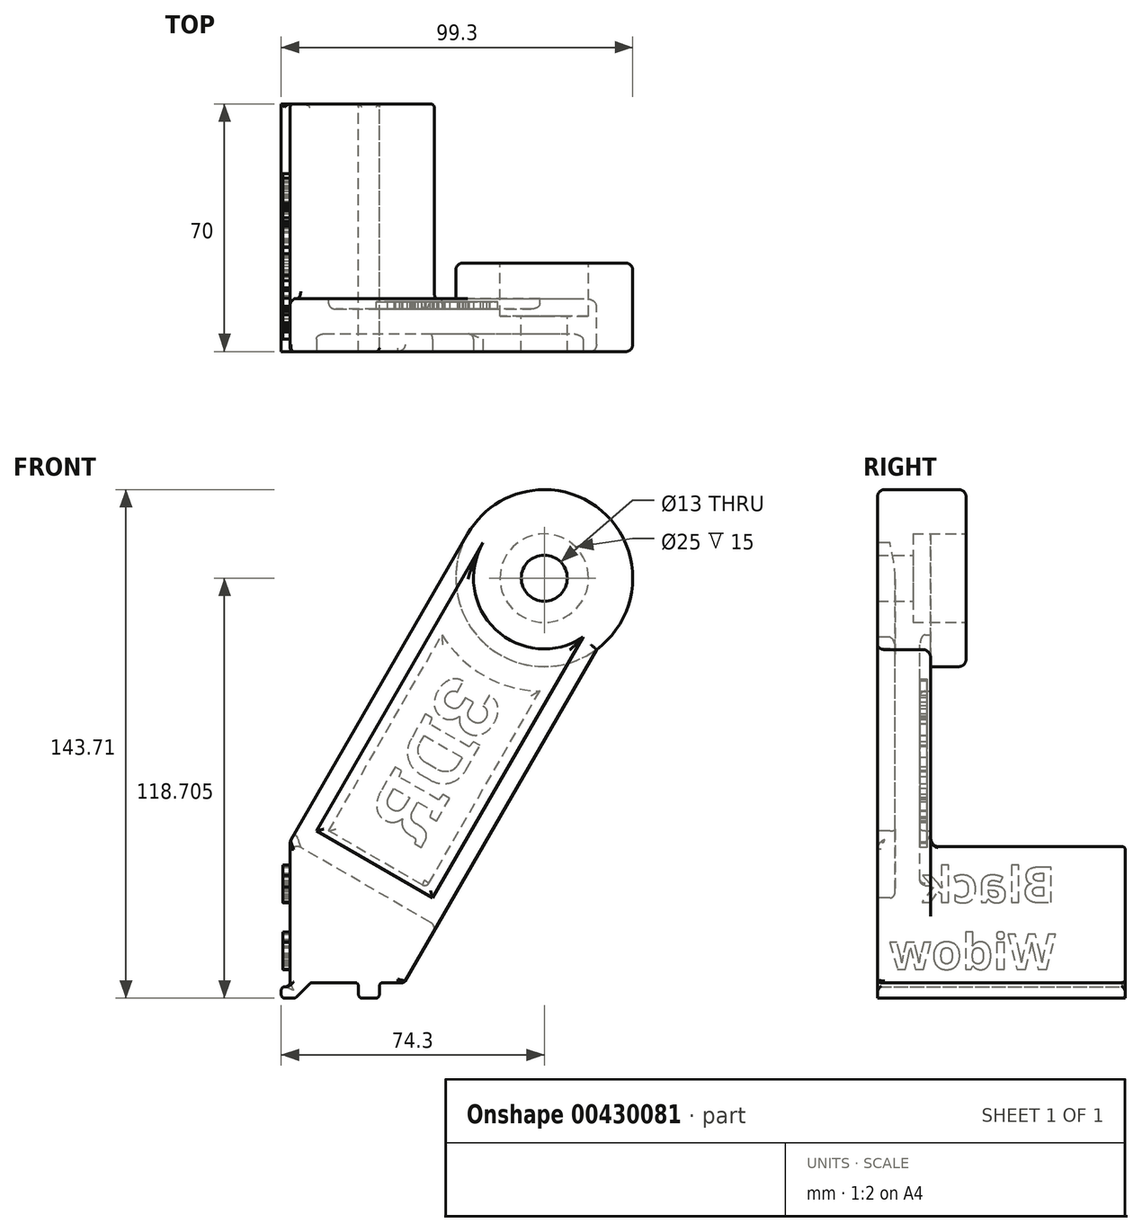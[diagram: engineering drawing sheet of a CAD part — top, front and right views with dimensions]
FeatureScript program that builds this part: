
annotation { "Feature Type Name" : "Feature", "Feature Type Description" : "" }
export const myFeature = defineFeature(function(context is Context, id is Id, definition is map)
    precondition{}
    {
        {
            var Q0;
            Q0=qCreatedBy(makeId("Front.planeOp"),FACE);
            var sketch = newSketch(context, id + "F0", { "sketchPlane" : qUnion([Q0])});
            skLineSegment(sketch, "E0", {"start": v(0, 0) * mm, "end": v(13.54, 0) * mm});
            skLineSegment(sketch, "E1", {"start": v(13.54, 0) * mm, "end": v(13.54, -4.39) * mm});
            skLineSegment(sketch, "E2", {"start": v(13.54, -4.39) * mm, "end": v(19.4, -4.39) * mm});
            skLineSegment(sketch, "E3", {"start": v(19.4, -4.39) * mm, "end": v(19.4, 0) * mm});
            skLineSegment(sketch, "E4", {"start": v(19.4, 0) * mm, "end": v(26.4, 0) * mm});
            skLineSegment(sketch, "E5", {"start": v(0, 0) * mm, "end": v(-4.4, -4.4) * mm});
            skLineSegment(sketch, "E6", {"start": v(-4.4, -4.4) * mm, "end": v(-8.3, -4.4) * mm});
            skLineSegment(sketch, "E7", {"start": v(-8.3, -4.4) * mm, "end": v(-8.3, -1.14) * mm});
            skLineSegment(sketch, "E8", {"start": v(-8.3, -1.14) * mm, "end": v(-5.8, -1.14) * mm});
            skLineSegment(sketch, "E9", {"start": v(-5.8, -1.14) * mm, "end": v(-5.8, 39.95) * mm});
            skLineSegment(sketch, "E10", {"start": v(26.4, 0) * mm, "end": v(80.74, 94.13) * mm});
            skLineSegment(sketch, "E11", {"start": v(0, 0) * mm, "end": v(66, 114.32) * mm, "construction": true});
            skCircle(sketch, "E12", {"center": v(66, 114.32) * mm, "radius": 95 * mm, "construction": true});
            skLineSegment(sketch, "E13", {"start": v(-5.8, 39.95) * mm, "end": v(44.35, 126.82) * mm});
            skCircle(sketch, "E14", {"center": v(66, 114.32) * mm, "radius": 6.5 * mm});
            skCircle(sketch, "E15", {"center": v(66, 114.32) * mm, "radius": 25 * mm});
            skSolve(sketch);
        }
        {
            var Q0;
            Q0 = qSketchRegion(id + "F0", true);
            extrude(context, id + "F1", {"entities" : qUnion([Q0]), "depth" : 70 * mm});
        }
        {
            var Q0;
            Q0=makeQuery(id+"F1.opExtrude","SWEPT_FACE",FACE,{"disambiguationData":[OSD([sQuery(id+"F0.wireOp",EDGE,"E13")])]});
            var sketch = newSketch(context, id + "F2", { "sketchPlane" : qUnion([Q0])});
            skLineSegment(sketch, "E16.0", {"start": v(70, 31.7) * mm, "end": v(70, 132) * mm, "construction": true});
            skLineSegment(sketch, "E17", {"start": v(55, 31.7) * mm, "end": v(55, 132) * mm});
            skLineSegment(sketch, "E18", {"start": v(55, 31.7) * mm, "end": v(0, 31.7) * mm});
            skLineSegment(sketch, "E19", {"start": v(0, 31.7) * mm, "end": v(0, 132) * mm});
            skLineSegment(sketch, "E20", {"start": v(0, 132) * mm, "end": v(0, 172) * mm});
            skLineSegment(sketch, "E21", {"start": v(0, 172) * mm, "end": v(55, 172) * mm});
            skLineSegment(sketch, "E22", {"start": v(55, 132) * mm, "end": v(55, 172) * mm});
            skSolve(sketch);
        }
        {
            var Q0;
            {var subQ0=sQuery(id+"F2.wireOp",EDGE,"E20");Q0=makeQuery(id+"F2.imprint","IMPRINT",FACE,{"disambiguationData":[TD([[makeQuery(id+"F2.imprint","IMPRINT",EDGE,{"derivedFrom":subQ0}),-1.0]])]});}
            var Q1;
            {var subQ0=sQuery(id+"F2.wireOp",EDGE,"E17");Q1=makeQuery(id+"F2.imprint","IMPRINT",FACE,{"disambiguationData":[TD([[makeQuery(id+"F2.imprint","IMPRINT",EDGE,{"derivedFrom":subQ0}),1.0]])]});}
            extrude(context, id + "F3", {"entities" : qUnion([Q0, Q1]), "operationType" : NewBodyOperationType.REMOVE, "endBound" : BoundingType.THROUGH_ALL, "oppositeDirection" : true, "depth" : 25 * mm});
        }
        {
            var Q0;
            Q0=makeQuery(id+"F3.boolean.opBoolean","COPY",FACE,{"derivedFrom":makeQuery(id+"F3.opExtrude","SWEPT_FACE",FACE,{"disambiguationData":[OSD([sQuery(id+"F2.wireOp",EDGE,"E17"),sQuery(id+"F2.wireOp",EDGE,"E22")])]})});
            var sketch = newSketch(context, id + "F4", { "sketchPlane" : qUnion([Q0])});
            skCircle(sketch, "E23", {"center": v(-66, 114.32) * mm, "radius": 25 * mm});
            skSolve(sketch);
        }
        {
            var Q0;
            Q0 = qSketchRegion(id + "F4", true);
            extrude(context, id + "F5", {"entities" : qUnion([Q0]), "operationType" : NewBodyOperationType.ADD, "depth" : 10 * mm});
        }
        {
            var Q0;
            Q0=makeQuery(id+"F5.opExtrude","CAP_FACE",FACE,{"disambiguationData":[OSD([sQuery(id+"F4.wireOp",EDGE,"E23")])],"isStart":false});
            var sketch = newSketch(context, id + "F6", { "sketchPlane" : qUnion([Q0])});
            skCircle(sketch, "E24", {"center": v(-66, 114.32) * mm, "radius": 12.5 * mm});
            skSolve(sketch);
        }
        {
            var Q0;
            Q0 = qSketchRegion(id + "F6", true);
            extrude(context, id + "F7", {"entities" : qUnion([Q0]), "operationType" : NewBodyOperationType.REMOVE, "oppositeDirection" : true, "depth" : 15 * mm});
        }
        {
            var Q0;
            Q0=makeQuery(id+"F3.boolean.opBoolean","COPY",FACE,{"derivedFrom":makeQuery(id+"F3.opExtrude","SWEPT_FACE",FACE,{"disambiguationData":[OSD([sQuery(id+"F2.wireOp",EDGE,"E17"),sQuery(id+"F2.wireOp",EDGE,"E22")])]})});
            var sketch = newSketch(context, id + "F8", { "sketchPlane" : qUnion([Q0])});
            skLineSegment(sketch, "E25.0", {"start": v(-5.13, 42.88) * mm, "end": v(-37.14, 98.32) * mm});
            skLineSegment(sketch, "E26.0", {"start": v(-32.72, 26.95) * mm, "end": v(-5.13, 42.88) * mm});
            skLineSegment(sketch, "E26.1", {"start": v(-32.72, 26.95) * mm, "end": v(-64.73, 82.39) * mm});
            skArc(sketch, "E26.2", {"start": v(-64.73, 82.39) * mm, "mid": v(-48.88, 86.8) * mm, "end": v(-37.14, 98.32) * mm});
            skSolve(sketch);
        }
        {
            var Q0;
            Q0 = qSketchRegion(id + "F8", true);
            extrude(context, id + "F9", {"entities" : qUnion([Q0]), "operationType" : NewBodyOperationType.REMOVE, "oppositeDirection" : true, "depth" : 3 * mm});
        }
        {
            var Q0;
            Q0=makeQuery(id+"F1.opExtrude","CAP_FACE",FACE,{"disambiguationData":[OSD([sQuery(id+"F0.wireOp",EDGE,"E0"),sQuery(id+"F0.wireOp",EDGE,"E1"),sQuery(id+"F0.wireOp",EDGE,"E2"),sQuery(id+"F0.wireOp",EDGE,"E3"),sQuery(id+"F0.wireOp",EDGE,"E4"),sQuery(id+"F0.wireOp",EDGE,"E5"),sQuery(id+"F0.wireOp",EDGE,"E6"),sQuery(id+"F0.wireOp",EDGE,"E7"),sQuery(id+"F0.wireOp",EDGE,"E8"),sQuery(id+"F0.wireOp",EDGE,"E9"),sQuery(id+"F0.wireOp",EDGE,"E10"),sQuery(id+"F0.wireOp",EDGE,"E13"),sQuery(id+"F0.wireOp",EDGE,"E14"),sQuery(id+"F0.wireOp",EDGE,"E15")])],"isStart":false});
            var sketch = newSketch(context, id + "F10", { "sketchPlane" : qUnion([Q0])});
            skLineSegment(sketch, "E27.0", {"start": v(34.44, 23.93) * mm, "end": v(76.97, 97.6) * mm});
            skLineSegment(sketch, "E27.2", {"start": v(1.65, 42.86) * mm, "end": v(48.68, 124.32) * mm});
            skLineSegment(sketch, "E28", {"start": v(1.65, 42.86) * mm, "end": v(34.44, 23.93) * mm});
            skArc(sketch, "E29", {"start": v(48.68, 124.32) * mm, "mid": v(52.27, 99.78) * mm, "end": v(76.97, 97.6) * mm});
            skSolve(sketch);
        }
        {
            var Q0;
            Q0=makeQuery(id+"F9.boolean.opBoolean","COPY",EDGE,{"derivedFrom":makeQuery(id+"F9.opExtrude","CAP_EDGE",EDGE,{"disambiguationData":[OSD([sQuery(id+"F8.wireOp",EDGE,"E26.2")])],"isStart":false})});
            var Q1;
            Q1=makeQuery(id+"F9.boolean.opBoolean","COPY",EDGE,{"derivedFrom":makeQuery(id+"F9.opExtrude","CAP_EDGE",EDGE,{"disambiguationData":[OSD([sQuery(id+"F8.wireOp",EDGE,"E26.1")])],"isStart":false})});
            var Q2;
            Q2=makeQuery(id+"F9.boolean.opBoolean","COPY",EDGE,{"derivedFrom":makeQuery(id+"F9.opExtrude","CAP_EDGE",EDGE,{"disambiguationData":[OSD([sQuery(id+"F8.wireOp",EDGE,"E25.0")])],"isStart":false})});
            var Q3;
            Q3=makeQuery(id+"F9.boolean.opBoolean","COPY",EDGE,{"derivedFrom":makeQuery(id+"F9.opExtrude","CAP_EDGE",EDGE,{"disambiguationData":[OSD([sQuery(id+"F8.wireOp",EDGE,"E26.0")])],"isStart":false})});
            var Q4;
            Q4=makeQuery(id+"FsvgU0utHE4NCiZ_1.boolean.opBoolean","COPY",EDGE,{"derivedFrom":makeQuery(id+"FsvgU0utHE4NCiZ_1.opExtrude","CAP_EDGE",EDGE,{"disambiguationData":[OSD([sQuery(id+"F10.wireOp",EDGE,"E27.0")])],"isStart":false})});
            var Q5;
            Q5=makeQuery(id+"FsvgU0utHE4NCiZ_1.boolean.opBoolean","COPY",FACE,{"derivedFrom":makeQuery(id+"FsvgU0utHE4NCiZ_1.opExtrude","CAP_FACE",FACE,{"disambiguationData":[OSD([sQuery(id+"F10.wireOp",EDGE,"E27.0"),sQuery(id+"F10.wireOp",EDGE,"E27.2"),sQuery(id+"F10.wireOp",EDGE,"E28"),sQuery(id+"F10.wireOp",EDGE,"E29")])],"isStart":false})});
            fillet(context, id + "F11", {"entities" : qUnion([Q0, Q1, Q2, Q3, Q4, Q5]), "radius" : 1.5 * mm, "tangentPropagation" : true, "allowEdgeOverflow" : false});
        }
        {
            var Q0;
            Q0=makeQuery(id+"F9.boolean.opBoolean","COPY",FACE,{"derivedFrom":makeQuery(id+"F9.opExtrude","CAP_FACE",FACE,{"disambiguationData":[OSD([sQuery(id+"F8.wireOp",EDGE,"E25.0"),sQuery(id+"F8.wireOp",EDGE,"E26.0"),sQuery(id+"F8.wireOp",EDGE,"E26.1"),sQuery(id+"F8.wireOp",EDGE,"E26.2")])],"isStart":false})});
            var sketch = newSketch(context, id + "F12", { "sketchPlane" : qUnion([Q0])});
            skText(sketch, "E30", { "text": "3DR", "fontName": "RobotoSlab-Bold.ttf"});
            skLineSegment(sketch, "E31", {"start": v(-19.68, 36.22) * mm, "end": v(-22.68, 41.41) * mm, "construction": true});
            const initialGuessF12  = {"E30": [-0.05498, 0.07937, 0.5, -0.86603, 0.018]};
            skSetInitialGuess(sketch, initialGuessF12);
            skSolve(sketch);
        }
        {
            var Q0;
            Q0 = qSketchRegion(id + "F12", true);
            extrude(context, id + "F13", {"entities" : qUnion([Q0]), "operationType" : NewBodyOperationType.ADD, "depth" : 2 * mm});
        }
        {
            var Q0;
            Q0=makeQuery(id+"F5.opExtrude","CAP_EDGE",EDGE,{"disambiguationData":[OSD([sQuery(id+"F4.wireOp",EDGE,"E23")])],"isStart":false});
            var Q1;
            Q1=makeQuery(id+"F1.opExtrude","CAP_EDGE",EDGE,{"disambiguationData":[OSD([sQuery(id+"F0.wireOp",EDGE,"E15")])],"isStart":false});
            var Q2;
            Q2=makeQuery(id+"F3.boolean.opBoolean","COPY",EDGE,{"derivedFrom":makeQuery(id+"F3.opExtrude","CAP_EDGE",EDGE,{"disambiguationData":[OSD([sQuery(id+"F2.wireOp",EDGE,"E17"),sQuery(id+"F2.wireOp",EDGE,"E22")])],"isStart":true})});
            var Q3;
            Q3=makeQuery(id+"F3.boolean.opBoolean","INTERSECT",EDGE,{"derivedFrom":[makeQuery(id+"F1.opExtrude","SWEPT_FACE",FACE,{"disambiguationData":[OSD([sQuery(id+"F0.wireOp",EDGE,"E10")])]}),makeQuery(id+"F3.opExtrude","SWEPT_FACE",FACE,{"disambiguationData":[OSD([sQuery(id+"F2.wireOp",EDGE,"E17"),sQuery(id+"F2.wireOp",EDGE,"E22")])]})]});
            var Q4;
            Q4=makeQuery(id+"F1.opExtrude","CAP_EDGE",EDGE,{"disambiguationData":[OSD([sQuery(id+"F0.wireOp",EDGE,"E10")])],"isStart":false});
            var Q5;
            Q5=makeQuery(id+"F3.boolean.opBoolean","INTERSECT",EDGE,{"derivedFrom":[makeQuery(id+"F1.opExtrude","SWEPT_FACE",FACE,{"disambiguationData":[OSD([sQuery(id+"F0.wireOp",EDGE,"E10")])]}),makeQuery(id+"F3.opExtrude","SWEPT_FACE",FACE,{"disambiguationData":[OSD([sQuery(id+"F2.wireOp",EDGE,"E18")])]})]});
            var Q6;
            Q6=makeQuery(id+"F3.boolean.opBoolean","MERGE",EDGE,{"derivedFrom":[makeQuery(id+"F1.opExtrude","SWEPT_EDGE",EDGE,{"disambiguationData":[OSD([sQuery(id+"F0.wireOp",EDGE,"E9"),sQuery(id+"F0.wireOp",EDGE,"E13")])]}),makeQuery(id+"F3.opExtrude","CAP_EDGE",EDGE,{"disambiguationData":[OSD([sQuery(id+"F2.wireOp",EDGE,"E18")])],"isStart":true})]});
            var Q7;
            Q7=makeQuery(id+"F5.opExtrude","CAP_EDGE",EDGE,{"disambiguationData":[OSD([sQuery(id+"F4.wireOp",EDGE,"E23")])],"isStart":true});
            var Q8;
            Q8=makeQuery(id+"F1.opExtrude","CAP_EDGE",EDGE,{"disambiguationData":[OSD([sQuery(id+"F0.wireOp",EDGE,"E13")])],"isStart":false});
            var Q9;
            Q9=makeQuery(id+"F3.boolean.opBoolean","COPY",EDGE,{"derivedFrom":makeQuery(id+"F3.opExtrude","SWEPT_EDGE",EDGE,{"disambiguationData":[OSD([sQuery(id+"F0.wireOp",EDGE,"E9"),sQuery(id+"F0.wireOp",EDGE,"E13"),sQuery(id+"F2.wireOp",EDGE,"E17"),sQuery(id+"F2.wireOp",EDGE,"E18")])]})});
            var Q10;
            Q10=makeQuery(id+"F3.boolean.opBoolean","COPY",EDGE,{"derivedFrom":makeQuery(id+"F3.opExtrude","SWEPT_EDGE",EDGE,{"disambiguationData":[OSD([sQuery(id+"F2.wireOp",EDGE,"E18"),sQuery(id+"F2.wireOp",EDGE,"E19")])]})});
            fillet(context, id + "F14", {"entities" : qUnion([Q0, Q1, Q2, Q3, Q4, Q5, Q6, Q7, Q8, Q9, Q10]), "radius" : 2 * mm, "tangentPropagation" : true, "allowEdgeOverflow" : false});
        }
        {
            var Q0;
            Q0=makeQuery(id+"F1.opExtrude","SWEPT_EDGE",EDGE,{"disambiguationData":[OSD([sQuery(id+"F0.wireOp",EDGE,"E0"),sQuery(id+"F0.wireOp",EDGE,"E1")])]});
            var Q1;
            Q1=makeQuery(id+"F1.opExtrude","SWEPT_EDGE",EDGE,{"disambiguationData":[OSD([sQuery(id+"F0.wireOp",EDGE,"E1"),sQuery(id+"F0.wireOp",EDGE,"E2")])]});
            var Q2;
            Q2=makeQuery(id+"F1.opExtrude","SWEPT_EDGE",EDGE,{"disambiguationData":[OSD([sQuery(id+"F0.wireOp",EDGE,"E2"),sQuery(id+"F0.wireOp",EDGE,"E3")])]});
            var Q3;
            Q3=makeQuery(id+"F1.opExtrude","SWEPT_EDGE",EDGE,{"disambiguationData":[OSD([sQuery(id+"F0.wireOp",EDGE,"E3"),sQuery(id+"F0.wireOp",EDGE,"E4")])]});
            var Q4;
            Q4=makeQuery(id+"F1.opExtrude","SWEPT_EDGE",EDGE,{"disambiguationData":[OSD([sQuery(id+"F0.wireOp",EDGE,"E4"),sQuery(id+"F0.wireOp",EDGE,"E10")])]});
            var Q5;
            Q5=makeQuery(id+"F1.opExtrude","SWEPT_EDGE",EDGE,{"disambiguationData":[OSD([sQuery(id+"F0.wireOp",EDGE,"E0"),sQuery(id+"F0.wireOp",EDGE,"E5")])]});
            var Q6;
            Q6=makeQuery(id+"F1.opExtrude","SWEPT_EDGE",EDGE,{"disambiguationData":[OSD([sQuery(id+"F0.wireOp",EDGE,"E5"),sQuery(id+"F0.wireOp",EDGE,"E6")])]});
            var Q7;
            Q7=makeQuery(id+"F1.opExtrude","SWEPT_EDGE",EDGE,{"disambiguationData":[OSD([sQuery(id+"F0.wireOp",EDGE,"E6"),sQuery(id+"F0.wireOp",EDGE,"E7")])]});
            var Q8;
            Q8=makeQuery(id+"F1.opExtrude","SWEPT_EDGE",EDGE,{"disambiguationData":[OSD([sQuery(id+"F0.wireOp",EDGE,"E7"),sQuery(id+"F0.wireOp",EDGE,"E8")])]});
            var Q9;
            Q9=makeQuery(id+"F1.opExtrude","CAP_EDGE",EDGE,{"disambiguationData":[OSD([sQuery(id+"F0.wireOp",EDGE,"E9")])],"isStart":false});
            var Q10;
            Q10=makeQuery(id+"F1.opExtrude","CAP_EDGE",EDGE,{"disambiguationData":[OSD([sQuery(id+"F0.wireOp",EDGE,"E9")])],"isStart":true});
            var Q11;
            Q11=makeQuery(id+"F1.opExtrude","CAP_EDGE",EDGE,{"disambiguationData":[OSD([sQuery(id+"F0.wireOp",EDGE,"E10")])],"isStart":true});
            var Q12;
            Q12=makeQuery(id+"F1.opExtrude","CAP_EDGE",EDGE,{"disambiguationData":[OSD([sQuery(id+"F0.wireOp",EDGE,"E0")])],"isStart":true});
            var Q13;
            Q13=makeQuery(id+"F1.opExtrude","CAP_EDGE",EDGE,{"disambiguationData":[OSD([sQuery(id+"F0.wireOp",EDGE,"E4")])],"isStart":true});
            var Q14;
            Q14=makeQuery(id+"F1.opExtrude","CAP_EDGE",EDGE,{"disambiguationData":[OSD([sQuery(id+"F0.wireOp",EDGE,"E2")])],"isStart":true});
            var Q15;
            Q15=makeQuery(id+"F1.opExtrude","CAP_EDGE",EDGE,{"disambiguationData":[OSD([sQuery(id+"F0.wireOp",EDGE,"E8")])],"isStart":true});
            fillet(context, id + "F15", {"entities" : qUnion([Q0, Q1, Q2, Q3, Q4, Q5, Q6, Q7, Q8, Q9, Q10, Q11, Q12, Q13, Q14, Q15]), "radius" : 1 * mm, "tangentPropagation" : true, "allowEdgeOverflow" : false});
        }
        {
            var Q0;
            Q0=makeQuery(id+"F9.boolean.opBoolean","COPY",EDGE,{"derivedFrom":makeQuery(id+"F9.opExtrude","CAP_EDGE",EDGE,{"disambiguationData":[OSD([sQuery(id+"F8.wireOp",EDGE,"E26.1")])],"isStart":true})});
            var Q1;
            Q1=makeQuery(id+"F11.opFillet","BLEND_EDGE",EDGE,{"blendedFrom":[makeQuery(id+"F9.boolean.opBoolean","COPY",EDGE,{"derivedFrom":makeQuery(id+"F9.opExtrude","CAP_EDGE",EDGE,{"disambiguationData":[OSD([sQuery(id+"F8.wireOp",EDGE,"E26.0")])],"isStart":false})}),makeQuery(id+"F9.boolean.opBoolean","COPY",EDGE,{"derivedFrom":makeQuery(id+"F9.opExtrude","CAP_EDGE",EDGE,{"disambiguationData":[OSD([sQuery(id+"F8.wireOp",EDGE,"E26.1")])],"isStart":false})})],"blendedInto":[]});
            var Q2;
            Q2=makeQuery(id+"F9.boolean.opBoolean","COPY",EDGE,{"derivedFrom":makeQuery(id+"F9.opExtrude","CAP_EDGE",EDGE,{"disambiguationData":[OSD([sQuery(id+"F8.wireOp",EDGE,"E26.2")])],"isStart":true})});
            var Q3;
            Q3=makeQuery(id+"F9.boolean.opBoolean","COPY",EDGE,{"derivedFrom":makeQuery(id+"F9.opExtrude","CAP_EDGE",EDGE,{"disambiguationData":[OSD([sQuery(id+"F8.wireOp",EDGE,"E25.0")])],"isStart":true})});
            var Q4;
            Q4=makeQuery(id+"F1.opExtrude","SWEPT_FACE",FACE,{"disambiguationData":[OSD([sQuery(id+"F0.wireOp",EDGE,"E9")])]});
            fillet(context, id + "F16", {"entities" : qUnion([Q0, Q1, Q2, Q3, Q4]), "radius" : 1.4 * mm, "tangentPropagation" : true, "allowEdgeOverflow" : false});
        }
        {
            var Q0;
            Q0=makeQuery(id+"F1.opExtrude","SWEPT_FACE",FACE,{"disambiguationData":[OSD([sQuery(id+"F0.wireOp",EDGE,"E9")])]});
            var sketch = newSketch(context, id + "F17", { "sketchPlane" : qUnion([Q0])});
            skText(sketch, "E32", { "text": "Black\nWidow", "fontName": "OpenSans-Bold.ttf"});
            const initialGuessF17  = {"E32": [0.01972, 0.02271, 1, 0, 0.01]};
            skSetInitialGuess(sketch, initialGuessF17);
            skSolve(sketch);
        }
        {
            var Q0;
            Q0 = qSketchRegion(id + "F17", true);
            extrude(context, id + "F18", {"entities" : qUnion([Q0]), "operationType" : NewBodyOperationType.ADD, "depth" : 2 * mm});
        }
        {
            var Q0;
            Q0 = qSketchRegion(id + "F10", true);
            extrude(context, id + "F19", {"entities" : qUnion([Q0]), "operationType" : NewBodyOperationType.REMOVE, "oppositeDirection" : true, "depth" : 5 * mm});
        }
        {
            var Q0;
            Q0=makeQuery(id+"F19.boolean.opBoolean","COPY",EDGE,{"derivedFrom":makeQuery(id+"F19.opExtrude","CAP_EDGE",EDGE,{"disambiguationData":[OSD([sQuery(id+"F10.wireOp",EDGE,"E27.2")])],"isStart":false})});
            var Q1;
            Q1=makeQuery(id+"F19.boolean.opBoolean","COPY",EDGE,{"derivedFrom":makeQuery(id+"F19.opExtrude","CAP_EDGE",EDGE,{"disambiguationData":[OSD([sQuery(id+"F10.wireOp",EDGE,"E28")])],"isStart":false})});
            var Q2;
            Q2=makeQuery(id+"F19.boolean.opBoolean","COPY",EDGE,{"derivedFrom":makeQuery(id+"F19.opExtrude","CAP_EDGE",EDGE,{"disambiguationData":[OSD([sQuery(id+"F10.wireOp",EDGE,"E27.0")])],"isStart":false})});
            var Q3;
            Q3=makeQuery(id+"F19.boolean.opBoolean","COPY",EDGE,{"derivedFrom":makeQuery(id+"F19.opExtrude","CAP_EDGE",EDGE,{"disambiguationData":[OSD([sQuery(id+"F10.wireOp",EDGE,"E29")])],"isStart":false})});
            fillet(context, id + "F20", {"entities" : qUnion([Q0, Q1, Q2, Q3]), "radius" : 1.5 * mm, "tangentPropagation" : true, "allowEdgeOverflow" : false});
        }
    });
